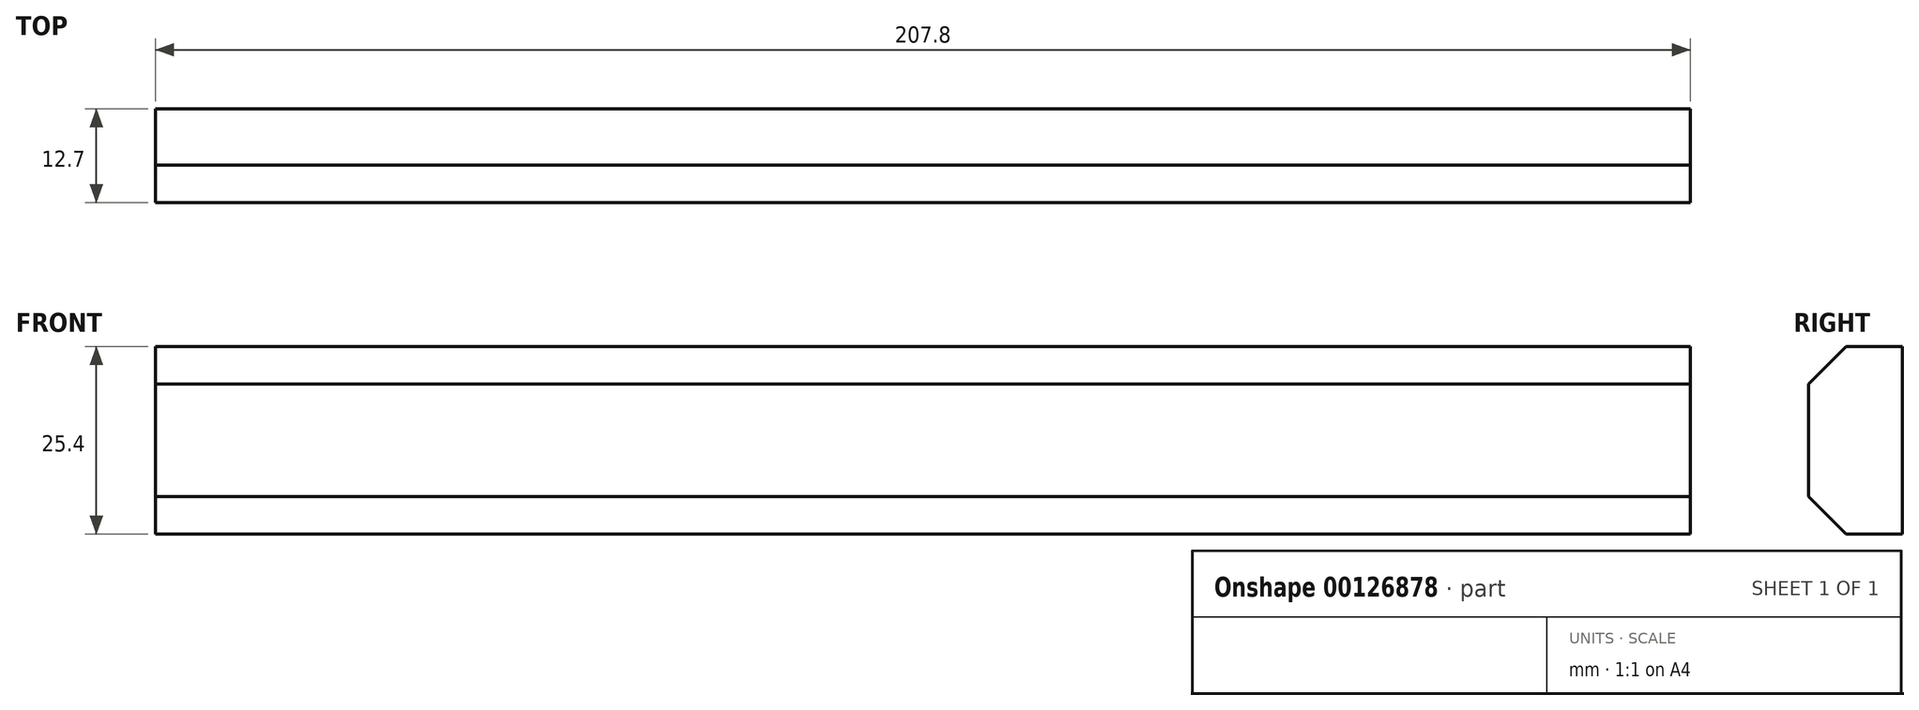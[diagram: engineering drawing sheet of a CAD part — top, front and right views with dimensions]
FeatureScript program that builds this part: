
annotation { "Feature Type Name" : "Feature", "Feature Type Description" : "" }
export const myFeature = defineFeature(function(context is Context, id is Id, definition is map)
    precondition{}
    {
        {
            var Q0;
            Q0=qCreatedBy(makeId("Front.planeOp"),FACE);
            var sketch = newSketch(context, id + "F0", { "sketchPlane" : qUnion([Q0])});
            skLineSegment(sketch, "E0.bottom", {"start": v(-110.27, -1.87) * mm, "end": v(97.53, -1.87) * mm});
            skLineSegment(sketch, "E0.top", {"start": v(-110.27, -27.27) * mm, "end": v(97.53, -27.27) * mm});
            skLineSegment(sketch, "E0.left", {"start": v(-110.27, -1.87) * mm, "end": v(-110.27, -27.27) * mm});
            skLineSegment(sketch, "E0.right", {"start": v(97.53, -1.87) * mm, "end": v(97.53, -27.27) * mm});
            skSolve(sketch);
        }
        {
            var Q0;
            Q0=makeQuery(id+"F0.imprint","IMPRINT",FACE,{"disambiguationData":[TD([[makeQuery(id+"F0.imprint","IMPRINT",EDGE,{"derivedFrom":sQuery(id+"F0.wireOp",EDGE,"E0.bottom")}),-1.0]])]});
            extrude(context, id + "F1", {"entities" : qUnion([Q0]), "depth" : 12.7 * mm});
        }
        {
            var Q0;
            Q0=makeQuery(id+"F1.opExtrude","CAP_EDGE",EDGE,{"disambiguationData":[OSD([sQuery(id+"F0.wireOp",EDGE,"E0.bottom")])],"isStart":false});
            var Q1;
            Q1=makeQuery(id+"F1.opExtrude","CAP_EDGE",EDGE,{"disambiguationData":[OSD([sQuery(id+"F0.wireOp",EDGE,"E0.top")])],"isStart":false});
            chamfer(context, id + "F2", {"entities" : qUnion([Q0, Q1]), "width" : 5.08 * mm, "tangentPropagation" : true});
        }
    });
